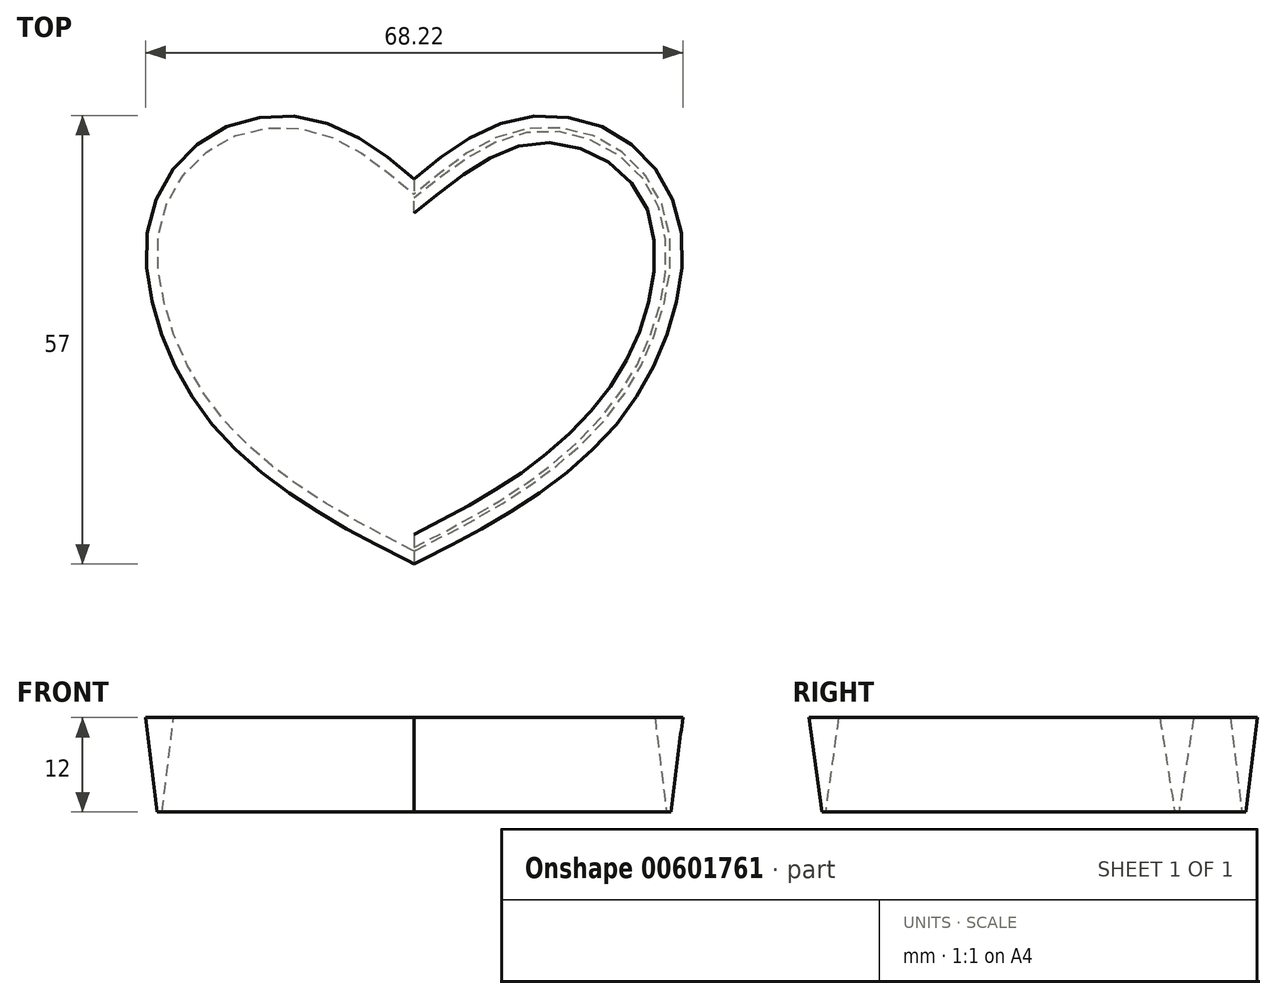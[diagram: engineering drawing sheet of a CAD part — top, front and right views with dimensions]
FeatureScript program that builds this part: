
annotation { "Feature Type Name" : "Feature", "Feature Type Description" : "" }
export const myFeature = defineFeature(function(context is Context, id is Id, definition is map)
    precondition{}
    {
        {
            var Q0;
            Q0=qCreatedBy(makeId("Top.planeOp"),FACE);
            var sketch = newSketch(context, id + "F0", { "sketchPlane" : qUnion([Q0])});
            skFitSpline(sketch, "E0", {"points": [v(0, 0) * mm, v(-6.18, 3.1) * mm, v(-11.32, 9.04) * mm, v(-12.35, 13.6) * mm, v(-8.98, 18.2) * mm, v(-3.64, 17.85) * mm, v(0, 14.57) * mm], "startDerivative": vector(-34.98, 13.49) * mm, "endDerivative": vector(20.93, -24.42) * mm});
            skFitSpline(sketch, "E1.MirrorCS", {"points": [v(0, 0) * mm, v(6.18, 3.1) * mm, v(11.32, 9.04) * mm, v(12.35, 13.6) * mm, v(8.98, 18.2) * mm, v(3.64, 17.85) * mm, v(0, 14.57) * mm], "startDerivative": vector(34.98, 13.49) * mm, "endDerivative": vector(-20.93, -24.42) * mm});
            skFitSpline(sketch, "E2", {"points": [v(0, -56.94) * mm, v(-4.57, -54.79) * mm, v(-9.81, -49.14) * mm, v(-11.83, -41.87) * mm, v(-7.26, -36.63) * mm, v(-1.88, -38.24) * mm, v(0, -40.4) * mm], "startDerivative": vector(-29.4, 10.65) * mm, "endDerivative": vector(12.34, -18.3) * mm});
            skFitSpline(sketch, "E3.MirrorCS", {"points": [v(0, -56.94) * mm, v(4.57, -54.79) * mm, v(9.81, -49.14) * mm, v(11.83, -41.87) * mm, v(7.26, -36.63) * mm, v(1.88, -38.24) * mm, v(0, -40.4) * mm], "startDerivative": vector(29.4, 10.65) * mm, "endDerivative": vector(-12.34, -18.3) * mm});
            skFitSpline(sketch, "E4", {"points": [v(0, -31.42) * mm, v(-5.74, -28.06) * mm, v(-10.58, -22.4) * mm, v(-10.99, -15) * mm, v(-5.74, -12.19) * mm, v(0, -15.28) * mm], "startDerivative": vector(-29.61, 15.21) * mm, "endDerivative": vector(27.92, -22.67) * mm});
            skFitSpline(sketch, "E5.MirrorCS", {"points": [v(0, -31.42) * mm, v(5.74, -28.06) * mm, v(10.58, -22.4) * mm, v(10.99, -15) * mm, v(5.74, -12.19) * mm, v(0, -15.28) * mm], "startDerivative": vector(29.61, 15.21) * mm, "endDerivative": vector(-27.92, -22.67) * mm});
            skFitSpline(sketch, "E6.0", {"points": [v(0.07, -31.55) * mm, v(0.68, -31.23) * mm, v(1.92, -30.6) * mm, v(3.75, -29.58) * mm, v(5.54, -28.42) * mm, v(7.27, -27.06) * mm, v(8.85, -25.47) * mm, v(9.97, -23.92) * mm, v(10.71, -22.52) * mm, v(11.17, -21.4) * mm, v(11.52, -20.24) * mm, v(11.82, -18.65) * mm, v(11.82, -17.08) * mm, v(11.47, -15.64) * mm, v(11, -14.66) * mm, v(10.32, -13.82) * mm, v(9.22, -12.88) * mm, v(7.88, -12.26) * mm, v(6.48, -12.01) * mm, v(5.44, -12.03) * mm, v(4.45, -12.25) * mm, v(3.17, -12.77) * mm, v(1.66, -13.75) * mm, v(0.5, -14.7) * mm, v(-0.1, -15.17) * mm]});
            skFitSpline(sketch, "E6.1", {"points": [v(-0.07, -31.55) * mm, v(-0.68, -31.23) * mm, v(-1.92, -30.6) * mm, v(-3.75, -29.58) * mm, v(-5.54, -28.42) * mm, v(-7.27, -27.06) * mm, v(-8.85, -25.47) * mm, v(-9.97, -23.92) * mm, v(-10.71, -22.52) * mm, v(-11.17, -21.4) * mm, v(-11.52, -20.24) * mm, v(-11.82, -18.65) * mm, v(-11.82, -17.08) * mm, v(-11.47, -15.64) * mm, v(-11, -14.66) * mm, v(-10.32, -13.82) * mm, v(-9.22, -12.88) * mm, v(-7.88, -12.26) * mm, v(-6.48, -12.01) * mm, v(-5.44, -12.03) * mm, v(-4.45, -12.25) * mm, v(-3.17, -12.77) * mm, v(-1.66, -13.75) * mm, v(-0.5, -14.7) * mm, v(0.1, -15.17) * mm]});
            skLineSegment(sketch, "E7", {"start": v(-0.07, -31.55) * mm, "end": v(2.38, -32.8) * mm});
            skLineSegment(sketch, "E8.MirrorCS", {"start": v(0.07, -31.55) * mm, "end": v(-2.38, -32.8) * mm});
            skSolve(sketch);
        }
        {
            var Q0;
            Q0=makeQuery(id+"F0.imprint","IMPRINT",FACE,{"disambiguationData":[TD([[makeQuery(id+"F0.imprint","IMPRINT",EDGE,{"derivedFrom":sQuery(id+"F0.wireOp",EDGE,"E4")}),1.0]])]});
            extrude(context, id + "F1", {"entities" : qUnion([Q0]), "depth" : (12 * 20 / 55) * mm, "offsetDistance" : 25 * mm, "hasDraft" : true, "draftAngle" : 7 * degree});
        }
        {
            var Q0;
            Q0=makeQuery(id+"F1.opExtrude","SWEPT_BODY",BODY,{"disambiguationData":[OSD([sQuery(id+"F0.wireOp",EDGE,"E4"),sQuery(id+"F0.wireOp",EDGE,"E5.MirrorCS"),sQuery(id+"F0.wireOp",EDGE,"E6.0"),sQuery(id+"F0.wireOp",EDGE,"E6.1"),sQuery(id+"F0.wireOp",EDGE,"E7"),sQuery(id+"F0.wireOp",EDGE,"E8.MirrorCS")])]});
            var Q1;
            Q1=makeQuery(id+"F1.opExtrude","CAP_VERTEX",VERTEX,{"disambiguationData":[OSD([sQuery(id+"F0.wireOp",EDGE,"E7"),sQuery(id+"F0.wireOp",EDGE,"E8.MirrorCS")])],"isStart":false});
            transform(context, id + "F2", {"entities" : qUnion([Q0]), "transformType" : TransformType.SCALE_UNIFORMLY, "scale" : 55 / 20, "scalePoint" : qUnion([Q1]), "makeCopy" : false});
        }
        {
            var Q0;
            Q0=makeQuery(id+"F1.opExtrude","CAP_FACE",FACE,{"disambiguationData":[OSD([sQuery(id+"F0.wireOp",EDGE,"E4"),sQuery(id+"F0.wireOp",EDGE,"E5.MirrorCS"),sQuery(id+"F0.wireOp",EDGE,"E6.0"),sQuery(id+"F0.wireOp",EDGE,"E6.1"),sQuery(id+"F0.wireOp",EDGE,"E7"),sQuery(id+"F0.wireOp",EDGE,"E8.MirrorCS")])],"isStart":true});
            var sketch = newSketch(context, id + "F3", { "sketchPlane" : qUnion([Q0])});
            skLineSegment(sketch, "E9", {"start": v(0, 30.08) * mm, "end": v(0, 30.53) * mm});
            skPoint(sketch, "E10", {"position": v(0, 30.3) * mm});
            skLineSegment(sketch, "E11", {"start": v(0, 30.3) * mm, "end": v(-0.18, 30.3) * mm});
            skSolve(sketch);
        }
        {
            var Q0;
            Q0=sQuery(id+"F3.wireOp",EDGE,"E11");
            cPlane(context, id + "F4", {"entities" : qUnion([Q0]), "cplaneType" : CPlaneType.LINE_ANGLE, "offset" : 25 * mm, "angle" : 0 * degree, "width" : 150 * mm, "height" : 150 * mm});
        }
    });
